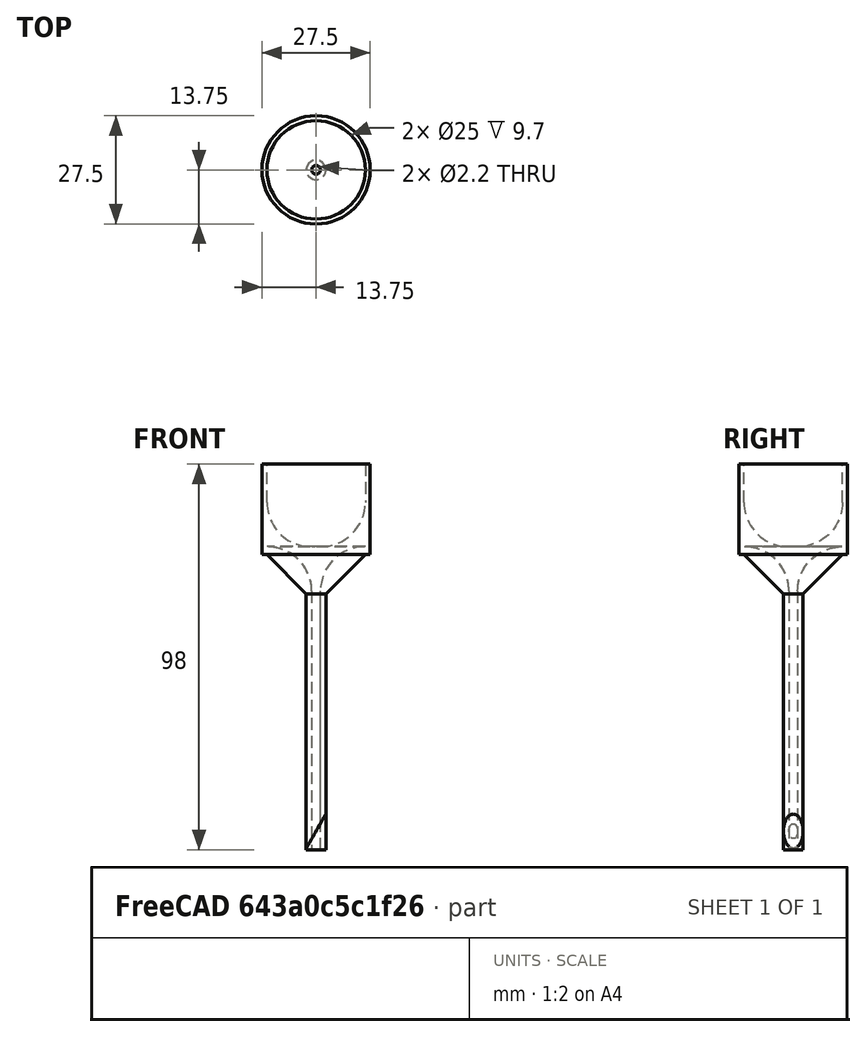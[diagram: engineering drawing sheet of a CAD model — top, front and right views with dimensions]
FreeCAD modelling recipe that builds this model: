
FCSTD DOCUMENT  (FreeCAD 0.19R)
Label: bottle neck
License: All rights reserved
LicenseURL: http://en.wikipedia.org/wiki/All_rights_reserved
objects: Sketcher::SketchObject×4, PartDesign::Pad×2, PartDesign::Pocket×2, PartDesign::Fillet×2, PartDesign::Chamfer×1, PartDesign::Body×1, Part::Box×1, Part::Cut×1
note: 21 computed .brp shape members not serialized (recipe doc carries the construction recipe); baked Part::Feature solids carry a one-line shape summary decoded from their .brp

FEATURE [Sketcher::SketchObject] Sketch
  FullyConstrained = true
  MapMode = 5
  Support = -> [XY_Plane]
  sketch-geometry (1):
    g0: Circle CenterX=0 CenterY=0 CenterZ=0 NormalX=0 NormalY=0 NormalZ=1 AngleXU=0 Radius=13.75
  constraints (2):
    c: Coincident(g0,g-1)
    c: Diameter(g0) = 27.5
FEATURE [PartDesign::Pad] Pad
  Direction = (1,1,1)
  Length = 23
  Length2 = 100
  Profile = -> Sketch
  Type = 0
FEATURE [Sketcher::SketchObject] Sketch001
  FullyConstrained = true
  MapMode = 5
  Placement = pos=(0,0,23) rot=(0,0,1;0rad)
  Support = -> [Pad]
  sketch-geometry (1):
    g0: Circle CenterX=0 CenterY=0 CenterZ=0 NormalX=0 NormalY=0 NormalZ=1 AngleXU=0 Radius=12.5
  constraints (2):
    c: Coincident(g0,g-1)
    c: Diameter(g0) = 25
FEATURE [PartDesign::Pocket] Pocket
  BaseFeature = -> Pad
  Length = 21
  Length2 = 100
  Profile = -> Sketch001
  Type = 0
FEATURE [Sketcher::SketchObject] Sketch002  label="long tube"
  FullyConstrained = true
  MapMode = 5
  Placement = pos=(0,0,0) rot=(1,0,0;3.14159rad)
  Support = -> [Pocket]
  sketch-geometry (1):
    g0: Circle CenterX=0 CenterY=0 CenterZ=0 NormalX=0 NormalY=0 NormalZ=1 AngleXU=0 Radius=2.5
  constraints (2):
    c: Coincident(g0,g-1)
    c: Diameter(g0) = 5
FEATURE [PartDesign::Pad] Pad001
  BaseFeature = -> Pocket
  Direction = (1,1,1)
  Length = 75
  Length2 = 100
  Profile = -> Sketch002
  Type = 0
FEATURE [Sketcher::SketchObject] Sketch003
  FullyConstrained = true
  MapMode = 5
  Placement = pos=(0,0,-75) rot=(1,0,0;3.14159rad)
  Support = -> [Pad001]
  sketch-geometry (1):
    g0: Circle CenterX=0 CenterY=0 CenterZ=0 NormalX=0 NormalY=0 NormalZ=1 AngleXU=0 Radius=1.1
  constraints (2):
    c: Coincident(g0,g-1)
    c: Diameter(g0) = 2.2
FEATURE [PartDesign::Pocket] Pocket001
  BaseFeature = -> Pad001
  Length = 80
  Length2 = 100
  Profile = -> Sketch003
  Type = 0
FEATURE [PartDesign::Fillet] Fillet
  Base = -> Pocket001 [Face7]
  BaseFeature = -> Pocket001
  Radius = 11
  SupportTransform = false
FEATURE [PartDesign::Chamfer] Chamfer
  Angle = 45
  Base = -> Pocket001 [Edge4]
  BaseFeature = -> Pocket001
  ChamferType = 0
  FlipDirection = false
  Size = 10
  Size2 = 1
  SupportTransform = false
FEATURE [PartDesign::Fillet] Fillet001
  Base = -> Chamfer [Face9]
  BaseFeature = -> Chamfer
  Radius = 11.3
  SupportTransform = false
FEATURE [PartDesign::Body] Body
  Group = -> [Sketch,Pad,Sketch001,Pocket,Sketch002,Pad001,Sketch003,Pocket001,Fillet,Chamfer,Fillet001]
  Origin = -> Origin
  Tip = -> Fillet001
FEATURE [Part::Box] Box  label="Cube"
  AttacherType = Attacher::AttachEngine3D
  Height = 5
  Length = 18
  Placement = pos=(-1,-4,-82) rot=(0,1,0;-1.0472rad)
  Width = 10
FEATURE [Part::Cut] Cut
  Base = -> Fillet001
  Tool = -> Box
